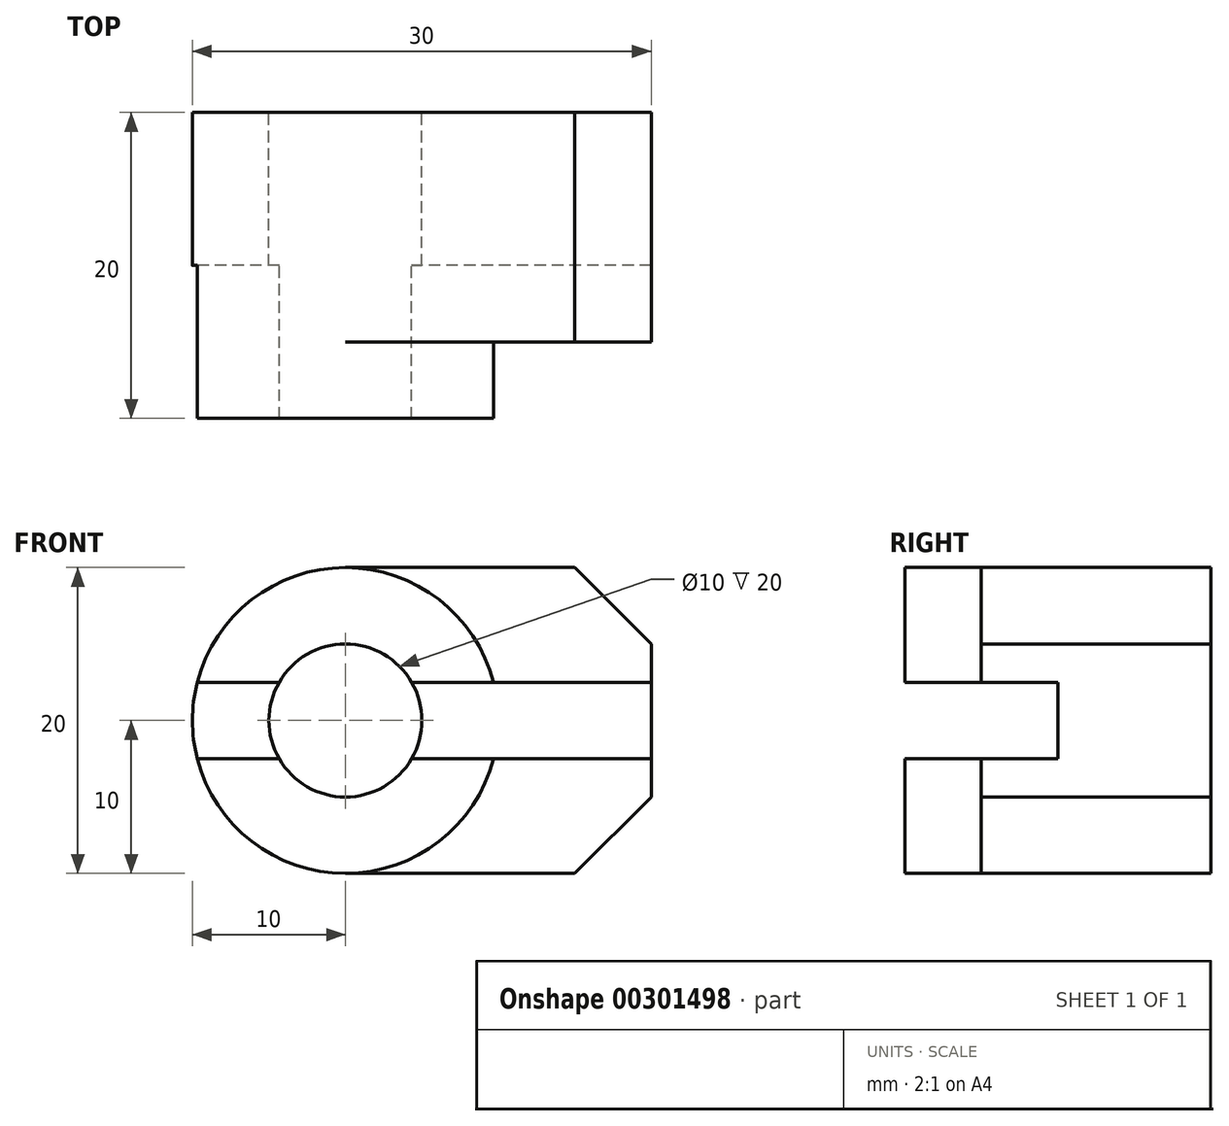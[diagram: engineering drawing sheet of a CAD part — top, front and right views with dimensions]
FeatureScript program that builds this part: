
annotation { "Feature Type Name" : "Feature", "Feature Type Description" : "" }
export const myFeature = defineFeature(function(context is Context, id is Id, definition is map)
    precondition{}
    {
        {
            var Q0;
            Q0=qCreatedBy(makeId("Front.planeOp"),FACE);
            var sketch = newSketch(context, id + "F0", { "sketchPlane" : qUnion([Q0])});
            skLineSegment(sketch, "E0.bottom", {"start": v(0, 0) * mm, "end": v(30, 0) * mm});
            skLineSegment(sketch, "E0.top", {"start": v(0, 20) * mm, "end": v(30, 20) * mm});
            skLineSegment(sketch, "E0.left", {"start": v(0, 0) * mm, "end": v(0, 20) * mm});
            skLineSegment(sketch, "E0.right", {"start": v(30, 0) * mm, "end": v(30, 20) * mm});
            skSolve(sketch);
        }
        {
            var Q0;
            Q0=makeQuery(id+"F0.imprint","IMPRINT",FACE,{"disambiguationData":[TD([[makeQuery(id+"F0.imprint","IMPRINT",EDGE,{"derivedFrom":sQuery(id+"F0.wireOp",EDGE,"E0.bottom")}),1.0]])]});
            extrude(context, id + "F1", {"entities" : qUnion([Q0]), "depth" : 15 * mm});
        }
        {
            var Q0;
            Q0=makeQuery(id+"F1.opExtrude","CAP_FACE",FACE,{"disambiguationData":[OSD([sQuery(id+"F0.wireOp",EDGE,"E0.bottom"),sQuery(id+"F0.wireOp",EDGE,"E0.top"),sQuery(id+"F0.wireOp",EDGE,"E0.left"),sQuery(id+"F0.wireOp",EDGE,"E0.right")])],"isStart":false});
            var sketch = newSketch(context, id + "F2", { "sketchPlane" : qUnion([Q0])});
            skCircle(sketch, "E1", {"center": v(10, 10) * mm, "radius": 10 * mm});
            skCircle(sketch, "E2", {"center": v(10, 10) * mm, "radius": 5 * mm});
            skSolve(sketch);
        }
        {
            var Q0;
            {var subQ0=sQuery(id+"F2.wireOp",EDGE,"E1");var subQ1=makeQuery(id+"F2.imprint","INTERSECT",VERTEX,{"derivedFrom":[makeQuery(id+"F1.opExtrude","CAP_EDGE",EDGE,{"disambiguationData":[OSD([sQuery(id+"F0.wireOp",EDGE,"E0.left")])],"isStart":false}),subQ0]});Q0=makeQuery(id+"F2.imprint","IMPRINT",FACE,{"disambiguationData":[TD([[makeQuery(id+"F2.imprint","IMPRINT",EDGE,{"disambiguationData":[TD([[subQ1,1.0]])],"derivedFrom":subQ0}),1.0]])]});}
            extrude(context, id + "F3", {"entities" : qUnion([Q0]), "operationType" : NewBodyOperationType.ADD, "depth" : 5 * mm});
        }
        {
            var Q0;
            {var subQ0=sQuery(id+"F0.wireOp",EDGE,"E0.left");var subQ1=sQuery(id+"F0.wireOp",EDGE,"E0.top");var subQ2=makeQuery(id+"F1.opExtrude","CAP_FACE",FACE,{"disambiguationData":[OSD([sQuery(id+"F0.wireOp",EDGE,"E0.bottom"),subQ1,subQ0,sQuery(id+"F0.wireOp",EDGE,"E0.right")])],"isStart":false});Q0=makeQuery(id+"F3.boolean.opBoolean","SPLIT",FACE,{"disambiguationData":[TD([subQ2,makeQuery(id+"F1.opExtrude","SWEPT_FACE",FACE,{"disambiguationData":[OSD([subQ1])]}),makeQuery(id+"F1.opExtrude","SWEPT_FACE",FACE,{"disambiguationData":[OSD([subQ0])]}),makeQuery(id+"F3.opExtrude","SWEPT_FACE",FACE,{"disambiguationData":[OSD([sQuery(id+"F2.wireOp",EDGE,"E1")])]})])],"derivedFrom":subQ2});}
            var Q1;
            {var subQ0=sQuery(id+"F0.wireOp",EDGE,"E0.bottom");var subQ1=sQuery(id+"F0.wireOp",EDGE,"E0.left");var subQ2=makeQuery(id+"F1.opExtrude","CAP_FACE",FACE,{"disambiguationData":[OSD([subQ0,sQuery(id+"F0.wireOp",EDGE,"E0.top"),subQ1,sQuery(id+"F0.wireOp",EDGE,"E0.right")])],"isStart":false});Q1=makeQuery(id+"F3.boolean.opBoolean","SPLIT",FACE,{"disambiguationData":[TD([makeQuery(id+"F1.opExtrude","SWEPT_FACE",FACE,{"disambiguationData":[OSD([subQ0])]}),subQ2,makeQuery(id+"F1.opExtrude","SWEPT_FACE",FACE,{"disambiguationData":[OSD([subQ1])]}),makeQuery(id+"F3.opExtrude","SWEPT_FACE",FACE,{"disambiguationData":[OSD([sQuery(id+"F2.wireOp",EDGE,"E1")])]})])],"derivedFrom":subQ2});}
            extrude(context, id + "F4", {"entities" : qUnion([Q0, Q1]), "operationType" : NewBodyOperationType.REMOVE, "endBound" : BoundingType.THROUGH_ALL, "oppositeDirection" : true, "depth" : 25 * mm});
        }
        {
            var Q0;
            Q0=makeQuery(id+"F3.boolean.opBoolean","SPLIT",FACE,{"disambiguationData":[TD([makeQuery(id+"F3.opExtrude","SWEPT_FACE",FACE,{"disambiguationData":[OSD([sQuery(id+"F2.wireOp",EDGE,"E2")])]})])],"derivedFrom":makeQuery(id+"F1.opExtrude","CAP_FACE",FACE,{"disambiguationData":[OSD([sQuery(id+"F0.wireOp",EDGE,"E0.bottom"),sQuery(id+"F0.wireOp",EDGE,"E0.top"),sQuery(id+"F0.wireOp",EDGE,"E0.left"),sQuery(id+"F0.wireOp",EDGE,"E0.right")])],"isStart":false})});
            extrude(context, id + "F5", {"entities" : qUnion([Q0]), "operationType" : NewBodyOperationType.REMOVE, "endBound" : BoundingType.THROUGH_ALL, "oppositeDirection" : true, "depth" : 25 * mm});
        }
        {
            var Q0;
            {var subQ0=sQuery(id+"F0.wireOp",EDGE,"E0.top");var subQ1=sQuery(id+"F0.wireOp",EDGE,"E0.right");var subQ2=sQuery(id+"F0.wireOp",EDGE,"E0.bottom");var subQ3=makeQuery(id+"F1.opExtrude","CAP_FACE",FACE,{"disambiguationData":[OSD([subQ2,subQ0,sQuery(id+"F0.wireOp",EDGE,"E0.left"),subQ1])],"isStart":false});Q0=makeQuery(id+"F3.boolean.opBoolean","SPLIT",FACE,{"disambiguationData":[TD([makeQuery(id+"F1.opExtrude","SWEPT_FACE",FACE,{"disambiguationData":[OSD([subQ2])]}),subQ3,makeQuery(id+"F1.opExtrude","SWEPT_FACE",FACE,{"disambiguationData":[OSD([subQ0])]}),makeQuery(id+"F1.opExtrude","SWEPT_FACE",FACE,{"disambiguationData":[OSD([subQ1])]}),makeQuery(id+"F3.opExtrude","SWEPT_FACE",FACE,{"disambiguationData":[OSD([sQuery(id+"F2.wireOp",EDGE,"E1")])]})])],"derivedFrom":subQ3});}
            var sketch = newSketch(context, id + "F6", { "sketchPlane" : qUnion([Q0])});
            skLineSegment(sketch, "E3.bottom", {"start": v(30, 12.5) * mm, "end": v(0, 12.5) * mm});
            skLineSegment(sketch, "E3.top", {"start": v(30, 7.5) * mm, "end": v(0, 7.5) * mm});
            skLineSegment(sketch, "E3.left", {"start": v(30, 12.5) * mm, "end": v(30, 7.5) * mm});
            skLineSegment(sketch, "E3.right", {"start": v(0, 12.5) * mm, "end": v(0, 7.5) * mm});
            skSolve(sketch);
        }
        {
            var Q0;
            {var subQ0=sQuery(id+"F6.wireOp",EDGE,"E3.left");Q0=makeQuery(id+"F6.imprint","IMPRINT",FACE,{"disambiguationData":[TD([[makeQuery(id+"F6.imprint","IMPRINT",EDGE,{"derivedFrom":subQ0}),1.0]])]});}
            var Q1;
            {var subQ0=sQuery(id+"F6.wireOp",EDGE,"E3.right");Q1=makeQuery(id+"F6.imprint","IMPRINT",FACE,{"disambiguationData":[TD([[makeQuery(id+"F6.imprint","IMPRINT",EDGE,{"derivedFrom":subQ0}),1.0]])]});}
            extrude(context, id + "F7", {"entities" : qUnion([Q0, Q1]), "operationType" : NewBodyOperationType.REMOVE, "oppositeDirection" : true, "depth" : 5 * mm, "hasSecondDirection" : true, "secondDirectionOppositeDirection" : false, "secondDirectionDepth" : 10 * mm});
        }
        {
            var Q0;
            Q0=makeQuery(id+"F1.opExtrude","SWEPT_EDGE",EDGE,{"disambiguationData":[OSD([sQuery(id+"F0.wireOp",EDGE,"E0.top"),sQuery(id+"F0.wireOp",EDGE,"E0.right")])]});
            var Q1;
            Q1=makeQuery(id+"F1.opExtrude","SWEPT_EDGE",EDGE,{"disambiguationData":[OSD([sQuery(id+"F0.wireOp",EDGE,"E0.bottom"),sQuery(id+"F0.wireOp",EDGE,"E0.right")])]});
            chamfer(context, id + "F8", {"entities" : qUnion([Q0, Q1]), "width" : 5 * mm, "tangentPropagation" : true});
        }
    });
